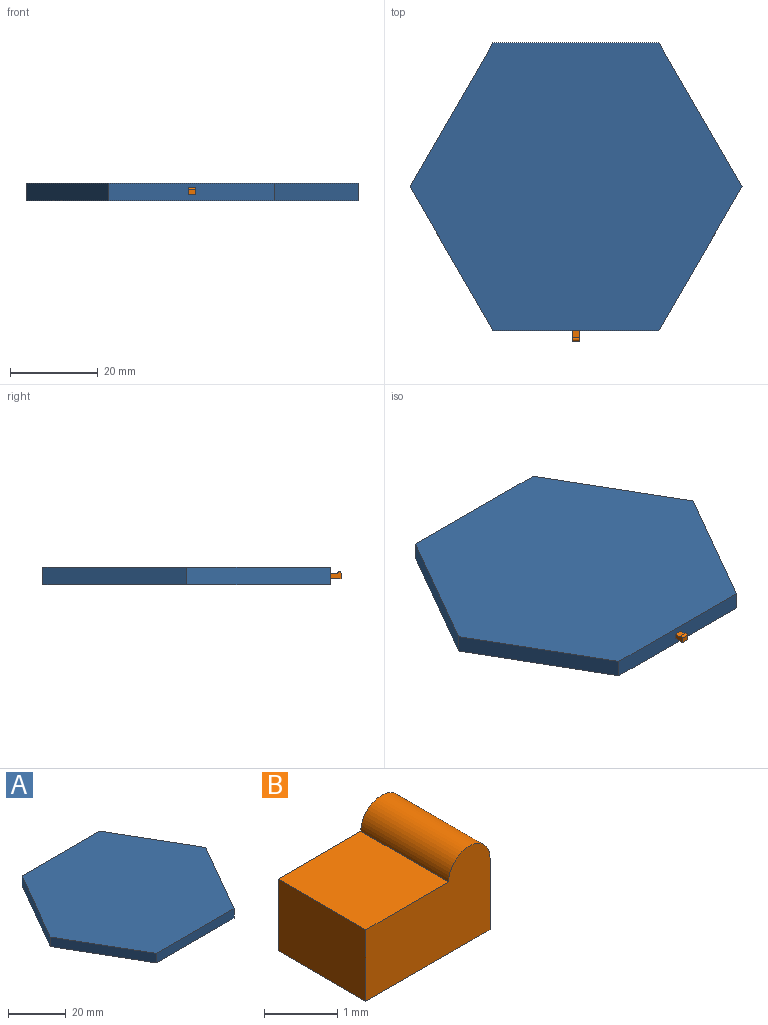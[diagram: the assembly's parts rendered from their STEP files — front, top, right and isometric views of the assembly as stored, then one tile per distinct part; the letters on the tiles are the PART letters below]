
ASSEMBLY  parts=2 mates=1
PART A: 8 faces, bbox 75.7x65.6x4 mm
  f0: plane 32.78x18.92mm, normal (0.87,0.5,0), area 151.4mm2, adj f1,f5,f6,f7
  f1: plane 37.85x4mm, normal (0,1,0), area 151.4mm2, adj f0,f2,f6,f7
  f2: plane 32.78x18.92mm, normal (-0.87,0.5,0), area 151.4mm2, adj f1,f3,f6,f7
  f3: plane 32.78x18.92mm, normal (-0.87,-0.5,0), area 151.4mm2, adj f2,f4,f6,f7
  f4: plane 37.85x4mm, normal (0,-1,0), area 151.4mm2, adj f3,f5,f6,f7
  f5: plane 32.78x18.92mm, normal (0.87,-0.5,0), area 151.4mm2, adj f0,f4,f6,f7
  f6: plane 75.69x65.55mm, normal (0,0,1), area 3721.4mm2, adj f0,f1,f2,f3,f4,f5
  f7: plane 75.69x65.55mm, normal (0,0,-1), area 3721.4mm2, adj f0,f1,f2,f3,f4,f5
PART B: 7 faces, bbox 2.4x1.7x1.6 mm
  f0: plane 1.7x1.6mm, normal (0,0,1), area 2.7mm2, adj f1,f4,f5,f6
  f1: plane 1.7x1.2mm, normal (-1,0,0), area 2mm2, adj f0,f2,f5,f6
  f2: plane 2.4x1.7mm, normal (0,0,-1), area 4.1mm2, adj f1,f3,f5,f6
  f3: plane 1.7x1.2mm, normal (1,0,0), area 2mm2, adj f2,f4,f5,f6
  f4: cylinder r=0.4mm len=1.7mm, axis (0,1,0), area 2.1mm2, adj f0,f3,f5,f6
  f5: plane 2.4x1.6mm, normal (0,-1,0), area 3.1mm2, adj f0,f1,f2,f3,f4
  f6: plane 2.4x1.6mm, normal (0,1,0), area 3.1mm2, adj f0,f1,f2,f3,f4
PLACE A t=(-11.81,-3.54,2.92)mm
PLACE B rot(axis=(0,0,-1),90deg) t=(-10.96,-38.14,4.32)mm
MATE fastened B.f1 <-> A.f4  axis (0,1,0) through (-11.81,-36.31,4.92)mm
